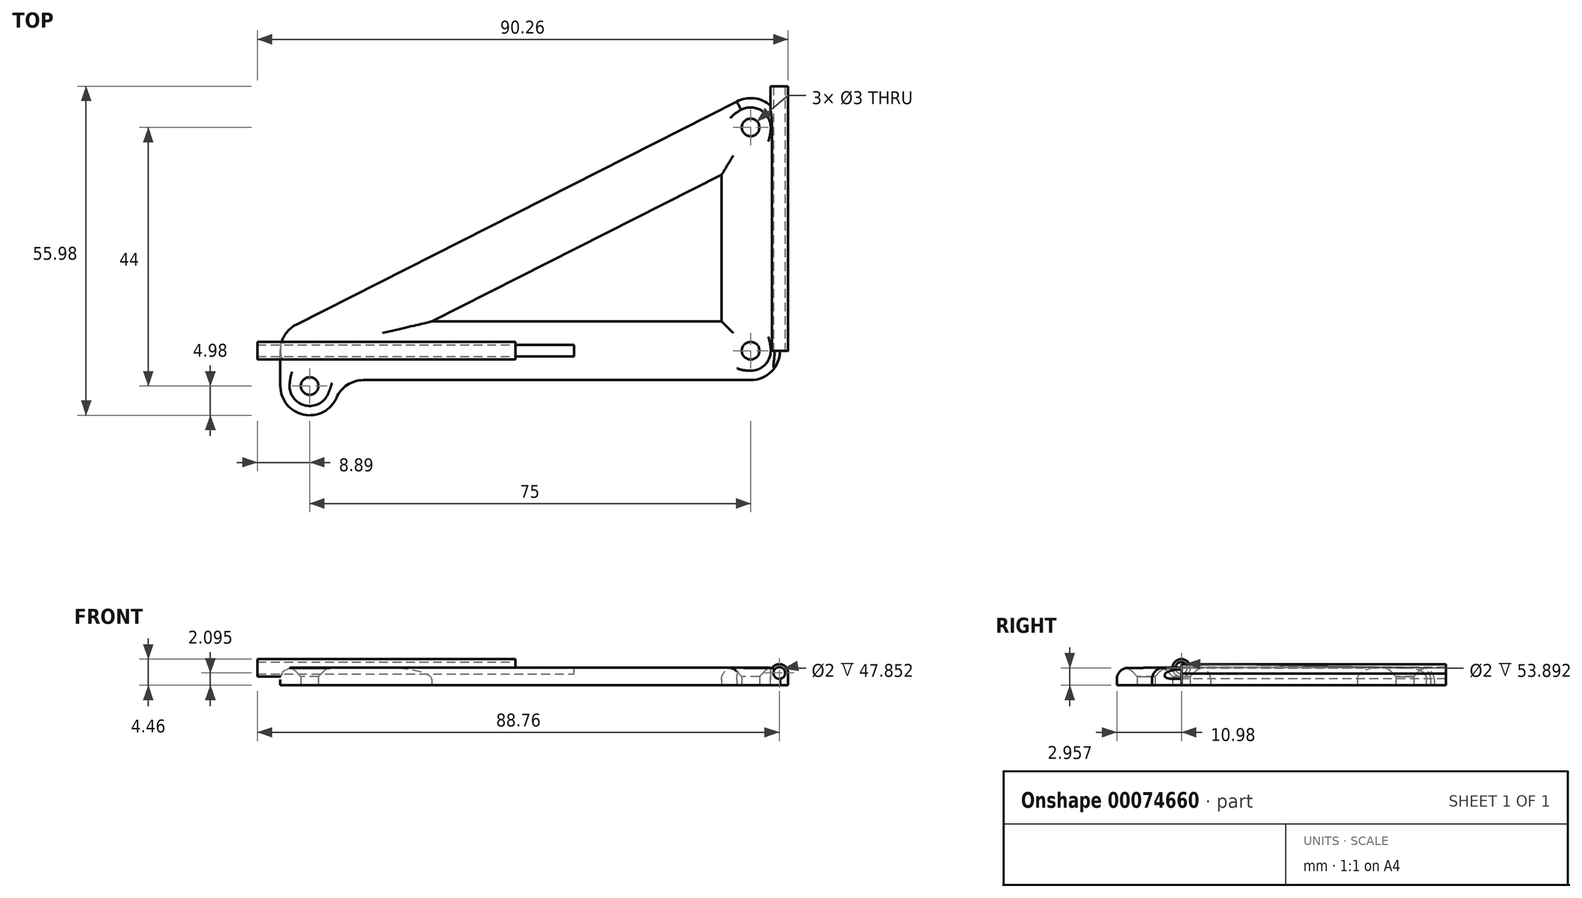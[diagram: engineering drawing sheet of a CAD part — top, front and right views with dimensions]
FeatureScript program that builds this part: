
annotation { "Feature Type Name" : "Feature", "Feature Type Description" : "" }
export const myFeature = defineFeature(function(context is Context, id is Id, definition is map)
    precondition{}
    {
        {
            var Q0;
            Q0=qCreatedBy(makeId("Top.planeOp"),FACE);
            var sketch = newSketch(context, id + "F0", { "sketchPlane" : qUnion([Q0])});
            skCircle(sketch, "E0", {"center": v(0, 0) * mm, "radius": 1.5 * mm});
            skCircle(sketch, "E1", {"center": v(0, 38) * mm, "radius": 1.5 * mm});
            skCircle(sketch, "E2", {"center": v(-75, -6) * mm, "radius": 1.5 * mm});
            skArc(sketch, "E3", {"start": v(-79.98, -6.02) * mm, "mid": v(-76.01, -10.87) * mm, "end": v(-70.44, -8) * mm});
            skArc(sketch, "E4", {"start": v(0, -5) * mm, "mid": v(3.54, -3.54) * mm, "end": v(5, 0) * mm});
            skArc(sketch, "E5", {"start": v(5, 38) * mm, "mid": v(2.57, 42.29) * mm, "end": v(-2.36, 42.41) * mm});
            skLineSegment(sketch, "E6", {"start": v(0, -5) * mm, "end": v(-65.86, -5) * mm});
            skLineSegment(sketch, "E7", {"start": v(-70.12, -5.04) * mm, "end": v(-70.12, -5) * mm});
            skLineSegment(sketch, "E8", {"start": v(-79.98, -6.02) * mm, "end": v(-80, 0) * mm});
            skLineSegment(sketch, "E9", {"start": v(-54.2, 5) * mm, "end": v(-4.95, 5) * mm});
            skLineSegment(sketch, "E10", {"start": v(5, 0) * mm, "end": v(5, 38) * mm});
            skLineSegment(sketch, "E11", {"start": v(-2.16, 42.5) * mm, "end": v(-77.27, 4.45) * mm});
            skLineSegment(sketch, "E12", {"start": v(-4.95, 29.95) * mm, "end": v(-4.95, 5) * mm});
            skPoint(sketch, "E13.trimOffspring.end.orphan", {"position": v(-4.95, 0) * mm});
            skPoint(sketch, "E14.trimOffspring.end.orphan", {"position": v(0, 5) * mm});
            skLineSegment(sketch, "E15.trimOffspring", {"start": v(-4.95, 29.95) * mm, "end": v(-54.2, 5) * mm});
            skPoint(sketch, "E16.center.orphan", {"position": v(-75, 0) * mm});
            skArc(sketch, "E17.trimOffspring", {"start": v(-77.25, 4.46) * mm, "mid": v(-79.26, 2.61) * mm, "end": v(-80, -0.02) * mm});
            skPoint(sketch, "E18.orphan", {"position": v(-70.12, 0) * mm});
            skPoint(sketch, "E19.visualSharp", {"position": v(-70.12, -5) * mm});
            skArc(sketch, "E19.filletArc", {"start": v(-65.86, -5) * mm, "mid": v(-68.6, -5.82) * mm, "end": v(-70.44, -8) * mm});
            skSolve(sketch);
        }
        {
            var Q0;
            Q0=qSketchRegion(id+"F0",true);
            extrude(context, id + "F1", {"entities" : qUnion([Q0]), "depth" : 3 * mm});
        }
        {
            var Q0;
            Q0=makeQuery(id+"F1.opExtrude","CAP_EDGE",EDGE,{"disambiguationData":[OSD([sQuery(id+"F0.wireOp",EDGE,"E2")])],"isStart":false});
            var Q1;
            Q1=makeQuery(id+"F1.opExtrude","CAP_EDGE",EDGE,{"disambiguationData":[OSD([sQuery(id+"F0.wireOp",EDGE,"E0")])],"isStart":false});
            var Q2;
            Q2=makeQuery(id+"F1.opExtrude","CAP_EDGE",EDGE,{"disambiguationData":[OSD([sQuery(id+"F0.wireOp",EDGE,"E1")])],"isStart":false});
            chamfer(context, id + "F2", {"entities" : qUnion([Q0, Q1, Q2]), "width" : 1.5 * mm, "tangentPropagation" : true});
        }
        {
            var Q0;
            Q0=makeQuery(id+"F1.opExtrude","CAP_FACE",FACE,{"disambiguationData":[OSD([sQuery(id+"F0.wireOp",EDGE,"E0"),sQuery(id+"F0.wireOp",EDGE,"E1"),sQuery(id+"F0.wireOp",EDGE,"E2"),sQuery(id+"F0.wireOp",EDGE,"E3"),sQuery(id+"F0.wireOp",EDGE,"E4"),sQuery(id+"F0.wireOp",EDGE,"E5"),sQuery(id+"F0.wireOp",EDGE,"E6"),sQuery(id+"F0.wireOp",EDGE,"E8"),sQuery(id+"F0.wireOp",EDGE,"E9"),sQuery(id+"F0.wireOp",EDGE,"E10"),sQuery(id+"F0.wireOp",EDGE,"E11"),sQuery(id+"F0.wireOp",EDGE,"E12"),sQuery(id+"F0.wireOp",EDGE,"E15.trimOffspring"),sQuery(id+"F0.wireOp",EDGE,"E17.trimOffspring"),sQuery(id+"F0.wireOp",EDGE,"E19.filletArc")])],"isStart":false});
            fillet(context, id + "F3", {"entities" : qUnion([Q0]), "radius" : 2 * mm, "tangentPropagation" : true, "allowEdgeOverflow" : false});
        }
        {
            var Q0;
            Q0=qCreatedBy(makeId("Front.planeOp"),FACE);
            var sketch = newSketch(context, id + "F4", { "sketchPlane" : qUnion([Q0])});
            skCircle(sketch, "E20", {"center": v(4.87, 2.1) * mm, "radius": 1 * mm});
            skArc(sketch, "E21", {"start": v(6.37, 2.02) * mm, "mid": v(4.9, 3.6) * mm, "end": v(3.37, 2.1) * mm});
            skLineSegment(sketch, "E22", {"start": v(6.37, 2.02) * mm, "end": v(6.37, 0) * mm});
            skLineSegment(sketch, "E23", {"start": v(6.37, 0) * mm, "end": v(3.38, 0) * mm});
            skLineSegment(sketch, "E24", {"start": v(3.38, 0) * mm, "end": v(3.37, 2.1) * mm});
            skSolve(sketch);
        }
        {
            var Q0;
            Q0=makeQuery(id+"F4.imprint","IMPRINT",FACE,{"disambiguationData":[TD([[makeQuery(id+"F4.imprint","IMPRINT",EDGE,{"derivedFrom":sQuery(id+"F4.wireOp",EDGE,"E20")}),-1.0]])]});
            extrude(context, id + "F5", {"entities" : qUnion([Q0]), "operationType" : NewBodyOperationType.ADD, "oppositeDirection" : true, "depth" : 45 * mm});
        }
        {
            var Q0;
            Q0=makeQuery(id+"F4.imprint","IMPRINT",FACE,{"disambiguationData":[TD([[makeQuery(id+"F4.imprint","IMPRINT",EDGE,{"derivedFrom":sQuery(id+"F4.wireOp",EDGE,"E20")}),1.0]])]});
            extrude(context, id + "F6", {"entities" : qUnion([Q0]), "operationType" : NewBodyOperationType.REMOVE, "endBound" : BoundingType.THROUGH_ALL, "oppositeDirection" : true, "depth" : 25 * mm, "hasSecondDirection" : true, "secondDirectionOppositeDirection" : false, "secondDirectionDepth" : 25 * mm});
        }
        {
            var Q0;
            Q0=qCreatedBy(makeId("Right.planeOp"),FACE);
            cPlane(context, id + "F7", {"entities" : qUnion([Q0]), "cplaneType" : CPlaneType.OFFSET, "offset" : 40 * mm, "oppositeDirection" : true, "width" : 150 * mm, "height" : 150 * mm});
        }
        {
            var Q0;
            Q0=qCreatedBy(id+"F7.planeOp",FACE);
            var sketch = newSketch(context, id + "F8", { "sketchPlane" : qUnion([Q0])});
            skCircle(sketch, "E25", {"center": v(0, 2.96) * mm, "radius": 1 * mm});
            skCircle(sketch, "E26", {"center": v(0, 2.96) * mm, "radius": 1.5 * mm});
            skSolve(sketch);
        }
        {
            var Q0;
            Q0=makeQuery(id+"F8.imprint","IMPRINT",FACE,{"disambiguationData":[TD([[makeQuery(id+"F8.imprint","IMPRINT",EDGE,{"derivedFrom":sQuery(id+"F8.wireOp",EDGE,"E25")}),-1.0]])]});
            extrude(context, id + "F9", {"entities" : qUnion([Q0]), "operationType" : NewBodyOperationType.ADD, "oppositeDirection" : true, "depth" : 43.9 * mm});
        }
        {
            var Q0;
            Q0=makeQuery(id+"F8.imprint","IMPRINT",FACE,{"disambiguationData":[TD([[makeQuery(id+"F8.imprint","IMPRINT",EDGE,{"derivedFrom":sQuery(id+"F8.wireOp",EDGE,"E25")}),1.0]])]});
            extrude(context, id + "F10", {"entities" : qUnion([Q0]), "operationType" : NewBodyOperationType.REMOVE, "endBound" : BoundingType.THROUGH_ALL, "oppositeDirection" : true, "depth" : 25 * mm, "hasSecondDirection" : true, "secondDirectionOppositeDirection" : false, "secondDirectionDepth" : 10 * mm});
        }
    });
